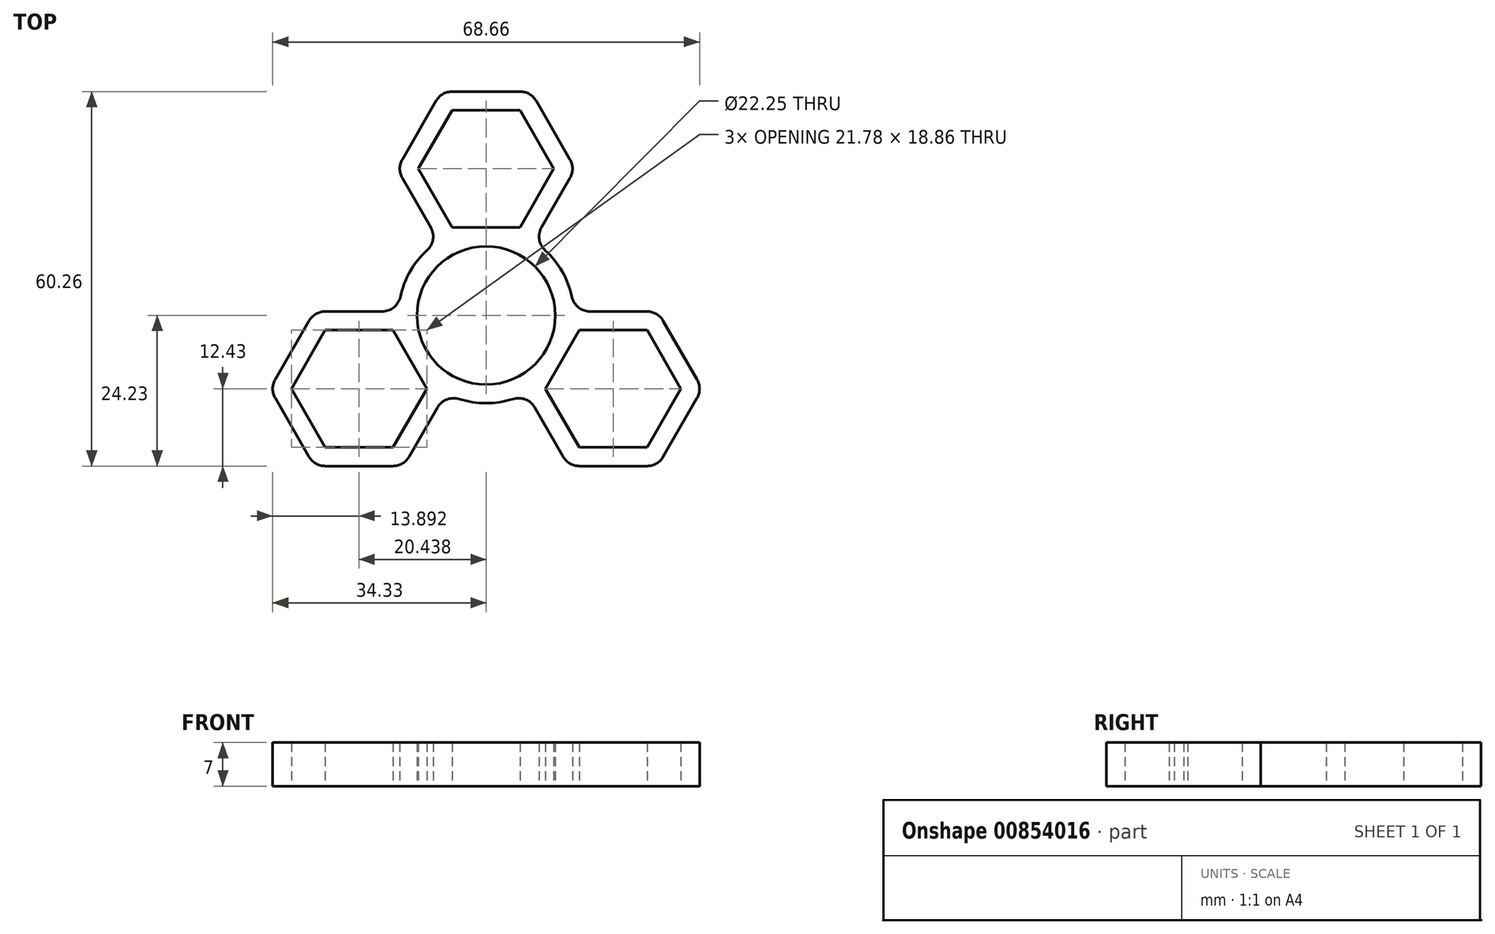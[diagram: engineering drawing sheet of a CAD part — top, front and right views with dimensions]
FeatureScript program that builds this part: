
annotation { "Feature Type Name" : "Feature", "Feature Type Description" : "" }
export const myFeature = defineFeature(function(context is Context, id is Id, definition is map)
    precondition{}
    {
        {
            var Q0;
            Q0=qCreatedBy(makeId("Top.planeOp"),FACE);
            var sketch = newSketch(context, id + "F0", { "sketchPlane" : qUnion([Q0])});
            skCircle(sketch, "E0", {"center": v(0, 0) * mm, "radius": 11.12 * mm});
            skLineSegment(sketch, "E1.0", {"start": v(-5.44, 33.03) * mm, "end": v(5.44, 33.03) * mm});
            skLineSegment(sketch, "E1.1", {"start": v(5.44, 33.03) * mm, "end": v(10.89, 23.6) * mm});
            skLineSegment(sketch, "E1.2", {"start": v(10.89, 23.6) * mm, "end": v(5.44, 14.17) * mm});
            skLineSegment(sketch, "E1.3", {"start": v(5.44, 14.17) * mm, "end": v(-5.44, 14.17) * mm});
            skLineSegment(sketch, "E1.4", {"start": v(-5.44, 14.17) * mm, "end": v(-10.89, 23.6) * mm});
            skLineSegment(sketch, "E1.5", {"start": v(-10.89, 23.6) * mm, "end": v(-5.44, 33.03) * mm});
            skPoint(sketch, "E1.0.midPoint", {"position": v(0, 33.03) * mm});
            skLineSegment(sketch, "E2.0", {"start": v(-5.44, 36.03) * mm, "end": v(5.44, 36.03) * mm});
            skLineSegment(sketch, "E2.1", {"start": v(8.04, 34.53) * mm, "end": v(13.49, 25.1) * mm});
            skLineSegment(sketch, "E2.2", {"start": v(13.49, 22.1) * mm, "end": v(8.91, 14.18) * mm});
            skLineSegment(sketch, "E2.4", {"start": v(-8.91, 14.18) * mm, "end": v(-13.49, 22.1) * mm});
            skLineSegment(sketch, "E2.5", {"start": v(-13.49, 25.1) * mm, "end": v(-8.04, 34.53) * mm});
            skPoint(sketch, "E2.0.midPoint", {"position": v(0, 36.03) * mm});
            skLineSegment(sketch, "E3.1.0", {"start": v(-15, -24.23) * mm, "end": v(-25.88, -24.23) * mm});
            skLineSegment(sketch, "E3.1.1", {"start": v(-25.88, 0.63) * mm, "end": v(-16.74, 0.63) * mm});
            skLineSegment(sketch, "E3.1.2", {"start": v(-7.82, -14.8) * mm, "end": v(-12.4, -22.73) * mm});
            skLineSegment(sketch, "E3.1.3", {"start": v(-31.33, -11.8) * mm, "end": v(-25.88, -2.37) * mm});
            skPoint(sketch, "E3.1.4", {"position": v(-28.6, -16.51) * mm});
            skLineSegment(sketch, "E3.1.5", {"start": v(-9.55, -11.8) * mm, "end": v(-15, -21.23) * mm});
            skLineSegment(sketch, "E3.1.6", {"start": v(-25.88, -2.37) * mm, "end": v(-15, -2.37) * mm});
            skLineSegment(sketch, "E3.1.7", {"start": v(-15, -21.23) * mm, "end": v(-25.88, -21.23) * mm});
            skLineSegment(sketch, "E3.1.8", {"start": v(-25.88, -21.23) * mm, "end": v(-31.33, -11.8) * mm});
            skPoint(sketch, "E3.1.9", {"position": v(-31.2, -18.01) * mm});
            skLineSegment(sketch, "E3.1.10", {"start": v(-33.93, -10.3) * mm, "end": v(-28.48, -0.87) * mm});
            skLineSegment(sketch, "E3.1.11", {"start": v(-28.48, -22.73) * mm, "end": v(-33.93, -13.3) * mm});
            skLineSegment(sketch, "E3.2.0", {"start": v(28.48, -0.87) * mm, "end": v(33.93, -10.3) * mm});
            skLineSegment(sketch, "E3.2.1", {"start": v(12.4, -22.73) * mm, "end": v(7.82, -14.8) * mm});
            skLineSegment(sketch, "E3.2.2", {"start": v(16.74, 0.63) * mm, "end": v(25.88, 0.63) * mm});
            skLineSegment(sketch, "E3.2.3", {"start": v(25.88, -21.23) * mm, "end": v(15, -21.23) * mm});
            skPoint(sketch, "E3.2.4", {"position": v(28.6, -16.52) * mm});
            skLineSegment(sketch, "E3.2.5", {"start": v(15, -2.37) * mm, "end": v(25.88, -2.37) * mm});
            skLineSegment(sketch, "E3.2.6", {"start": v(15, -21.23) * mm, "end": v(9.55, -11.8) * mm});
            skLineSegment(sketch, "E3.2.7", {"start": v(25.88, -2.37) * mm, "end": v(31.33, -11.8) * mm});
            skLineSegment(sketch, "E3.2.8", {"start": v(31.33, -11.8) * mm, "end": v(25.88, -21.23) * mm});
            skPoint(sketch, "E3.2.9", {"position": v(31.2, -18.02) * mm});
            skLineSegment(sketch, "E3.2.10", {"start": v(25.88, -24.23) * mm, "end": v(15, -24.23) * mm});
            skLineSegment(sketch, "E3.2.11", {"start": v(33.93, -13.3) * mm, "end": v(28.48, -22.73) * mm});
            skArc(sketch, "E4.0", {"start": v(-9.5, 10.46) * mm, "mid": v(-12.23, 7.06) * mm, "end": v(-13.8, 3) * mm});
            skArc(sketch, "E5.trimOffspring", {"start": v(-4.3, -13.45) * mm, "mid": v(0, -14.12) * mm, "end": v(4.3, -13.45) * mm});
            skArc(sketch, "E6.trimOffspring", {"start": v(13.8, 3) * mm, "mid": v(12.23, 7.06) * mm, "end": v(9.5, 10.46) * mm});
            skPoint(sketch, "E7.newPointA", {"position": v(7.18, 11.17) * mm});
            skArc(sketch, "E7.filletArc", {"start": v(8.91, 14.18) * mm, "mid": v(8.55, 12.22) * mm, "end": v(9.5, 10.46) * mm});
            skPoint(sketch, "E8.newPointA", {"position": v(13.26, 0.63) * mm});
            skArc(sketch, "E8.filletArc", {"start": v(13.8, 3) * mm, "mid": v(14.85, 1.3) * mm, "end": v(16.74, 0.63) * mm});
            skPoint(sketch, "E9.newPointA", {"position": v(6.09, -11.8) * mm});
            skArc(sketch, "E9.filletArc", {"start": v(7.82, -14.8) * mm, "mid": v(6.3, -13.51) * mm, "end": v(4.3, -13.45) * mm});
            skPoint(sketch, "E10.newPointA", {"position": v(-6.09, -11.8) * mm});
            skArc(sketch, "E10.filletArc", {"start": v(-4.3, -13.45) * mm, "mid": v(-6.3, -13.51) * mm, "end": v(-7.82, -14.8) * mm});
            skPoint(sketch, "E11.newPointA", {"position": v(-13.26, 0.63) * mm});
            skArc(sketch, "E11.filletArc", {"start": v(-16.74, 0.63) * mm, "mid": v(-14.85, 1.3) * mm, "end": v(-13.8, 3) * mm});
            skPoint(sketch, "E12.newPointB", {"position": v(-7.18, 11.17) * mm});
            skArc(sketch, "E12.filletArc", {"start": v(-9.5, 10.46) * mm, "mid": v(-8.55, 12.22) * mm, "end": v(-8.91, 14.18) * mm});
            skPoint(sketch, "E13.visualSharp", {"position": v(-14.35, 23.6) * mm});
            skArc(sketch, "E13.filletArc", {"start": v(-13.49, 25.1) * mm, "mid": v(-13.89, 23.6) * mm, "end": v(-13.49, 22.1) * mm});
            skPoint(sketch, "E14.visualSharp", {"position": v(-7.18, 36.03) * mm});
            skArc(sketch, "E14.filletArc", {"start": v(-5.44, 36.03) * mm, "mid": v(-6.94, 35.63) * mm, "end": v(-8.04, 34.53) * mm});
            skPoint(sketch, "E15.visualSharp", {"position": v(7.18, 36.03) * mm});
            skArc(sketch, "E15.filletArc", {"start": v(8.04, 34.53) * mm, "mid": v(6.94, 35.63) * mm, "end": v(5.44, 36.03) * mm});
            skPoint(sketch, "E16.visualSharp", {"position": v(14.35, 23.6) * mm});
            skArc(sketch, "E16.filletArc", {"start": v(13.49, 22.1) * mm, "mid": v(13.89, 23.6) * mm, "end": v(13.49, 25.1) * mm});
            skPoint(sketch, "E17.visualSharp", {"position": v(27.61, 0.63) * mm});
            skArc(sketch, "E17.filletArc", {"start": v(28.48, -0.87) * mm, "mid": v(27.38, 0.23) * mm, "end": v(25.88, 0.63) * mm});
            skPoint(sketch, "E18.visualSharp", {"position": v(34.8, -11.8) * mm});
            skArc(sketch, "E18.filletArc", {"start": v(33.93, -13.3) * mm, "mid": v(34.33, -11.8) * mm, "end": v(33.93, -10.3) * mm});
            skPoint(sketch, "E19.visualSharp", {"position": v(27.61, -24.23) * mm});
            skArc(sketch, "E19.filletArc", {"start": v(25.88, -24.23) * mm, "mid": v(27.38, -23.83) * mm, "end": v(28.48, -22.73) * mm});
            skPoint(sketch, "E20.visualSharp", {"position": v(13.26, -24.23) * mm});
            skArc(sketch, "E20.filletArc", {"start": v(12.4, -22.73) * mm, "mid": v(13.5, -23.83) * mm, "end": v(15, -24.23) * mm});
            skPoint(sketch, "E21.visualSharp", {"position": v(-13.26, -24.23) * mm});
            skArc(sketch, "E21.filletArc", {"start": v(-15, -24.23) * mm, "mid": v(-13.5, -23.83) * mm, "end": v(-12.4, -22.73) * mm});
            skPoint(sketch, "E22.visualSharp", {"position": v(-27.61, -24.23) * mm});
            skArc(sketch, "E22.filletArc", {"start": v(-28.48, -22.73) * mm, "mid": v(-27.38, -23.83) * mm, "end": v(-25.88, -24.23) * mm});
            skPoint(sketch, "E23.visualSharp", {"position": v(-34.8, -11.8) * mm});
            skArc(sketch, "E23.filletArc", {"start": v(-33.93, -10.3) * mm, "mid": v(-34.33, -11.8) * mm, "end": v(-33.93, -13.3) * mm});
            skPoint(sketch, "E24.visualSharp", {"position": v(-27.61, 0.63) * mm});
            skArc(sketch, "E24.filletArc", {"start": v(-25.88, 0.63) * mm, "mid": v(-27.38, 0.23) * mm, "end": v(-28.48, -0.87) * mm});
            skLineSegment(sketch, "E25", {"start": v(-15, -2.37) * mm, "end": v(-9.55, -11.8) * mm});
            skLineSegment(sketch, "E26", {"start": v(9.55, -11.8) * mm, "end": v(15, -2.37) * mm});
            skSolve(sketch);
        }
        {
            var Q0;
            Q0 = qSketchRegion(id + "F0", true);
            extrude(context, id + "F1", {"entities" : qUnion([Q0]), "depth" : 7 * mm, "offsetDistance" : 25 * mm});
        }
    });
